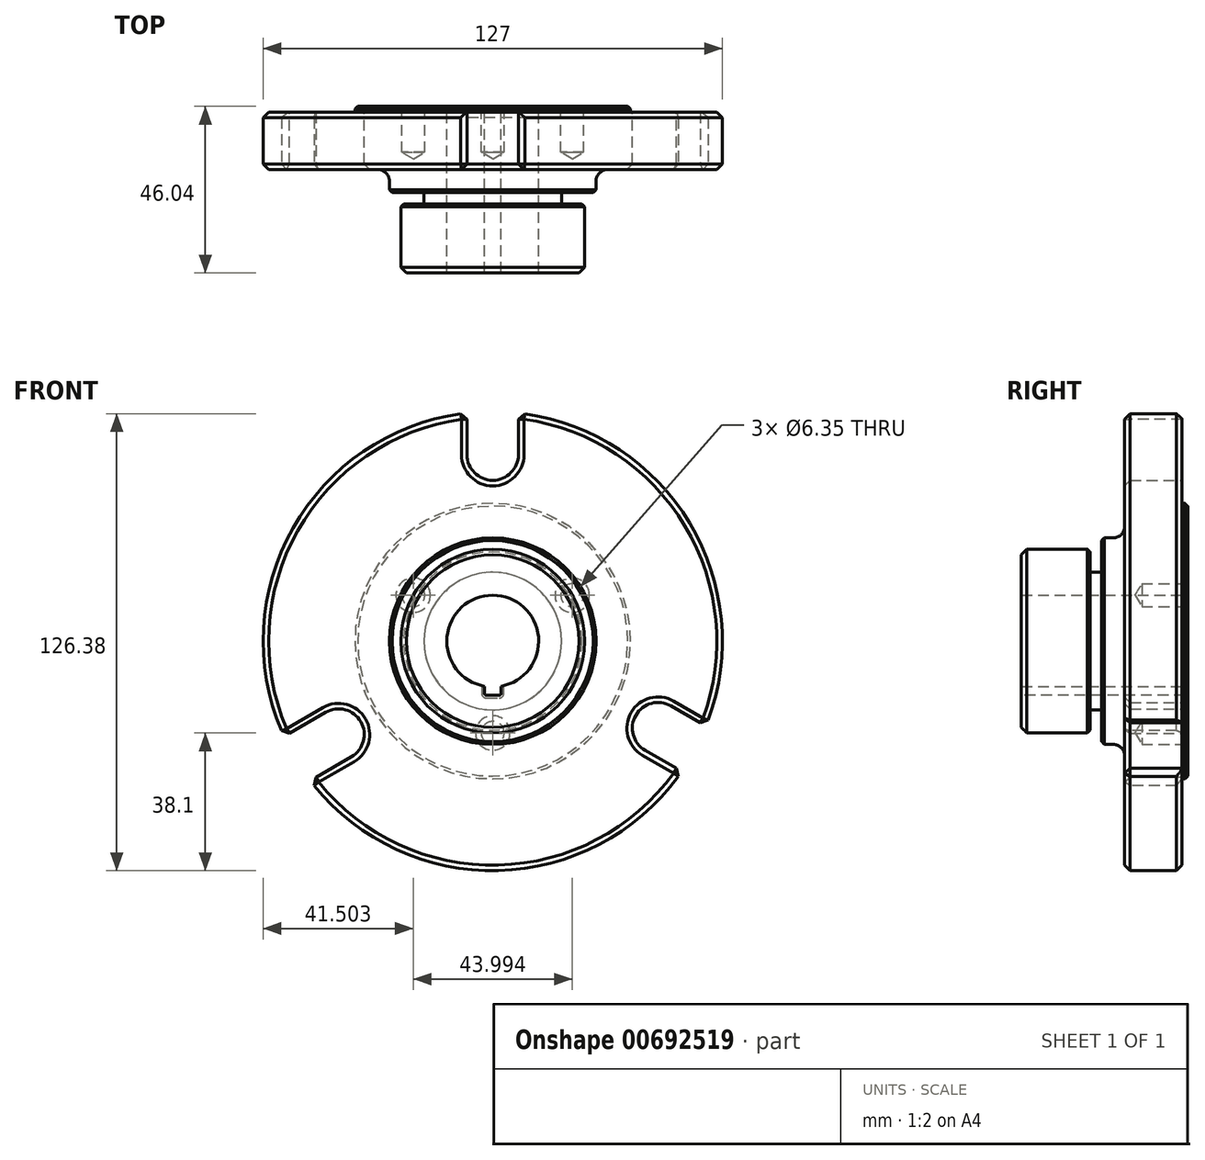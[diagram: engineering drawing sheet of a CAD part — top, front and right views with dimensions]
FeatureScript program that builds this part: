
annotation { "Feature Type Name" : "Feature", "Feature Type Description" : "" }
export const myFeature = defineFeature(function(context is Context, id is Id, definition is map)
    precondition{}
    {
        {
            var Q0;
            Q0=qCreatedBy(makeId("Right.planeOp"),FACE);
            var sketch = newSketch(context, id + "F0", { "sketchPlane" : qUnion([Q0])});
            skLineSegment(sketch, "E0", {"start": v(-17.46, 63.5) * mm, "end": v(-1.59, 63.5) * mm});
            skLineSegment(sketch, "E1", {"start": v(-1.59, 63.5) * mm, "end": v(-1.59, 38.1) * mm});
            skLineSegment(sketch, "E2", {"start": v(-1.59, 38.1) * mm, "end": v(0, 38.1) * mm});
            skLineSegment(sketch, "E3", {"start": v(0, 38.1) * mm, "end": v(0, 0) * mm});
            skLineSegment(sketch, "E4", {"start": v(0, 0) * mm, "end": v(-46.04, 0) * mm});
            skLineSegment(sketch, "E5", {"start": v(-46.04, 0) * mm, "end": v(-46.04, 25.4) * mm});
            skLineSegment(sketch, "E6", {"start": v(-46.04, 25.4) * mm, "end": v(-26.99, 25.4) * mm});
            skLineSegment(sketch, "E7", {"start": v(-26.99, 25.4) * mm, "end": v(-26.99, 19.05) * mm});
            skLineSegment(sketch, "E8", {"start": v(-26.99, 19.05) * mm, "end": v(-23.81, 19.05) * mm});
            skLineSegment(sketch, "E9", {"start": v(-23.81, 19.05) * mm, "end": v(-23.81, 28.58) * mm});
            skLineSegment(sketch, "E10", {"start": v(-23.81, 28.58) * mm, "end": v(-20.64, 28.58) * mm});
            skLineSegment(sketch, "E11", {"start": v(-17.46, 31.75) * mm, "end": v(-17.46, 63.5) * mm});
            skPoint(sketch, "E12.visualSharp", {"position": v(-17.46, 28.58) * mm});
            skArc(sketch, "E12.filletArc", {"start": v(-20.64, 28.57) * mm, "mid": v(-18.4, 29.5) * mm, "end": v(-17.46, 31.75) * mm});
            skLineSegment(sketch, "E13", {"start": v(-69.6, 0) * mm, "end": v(49.13, 0) * mm, "construction": true});
            skSolve(sketch);
        }
        {
            var Q0;
            Q0=makeQuery(id+"F0.imprint","IMPRINT",FACE,{"disambiguationData":[TD([[makeQuery(id+"F0.imprint","IMPRINT",EDGE,{"derivedFrom":sQuery(id+"F0.wireOp",EDGE,"E0")}),-1.0]])]});
            var Q1;
            Q1=sQuery(id+"F0.wireOp",EDGE,"E13");
            revolve(context, id + "F1", {"entities" : qUnion([Q0]), "axis" : qUnion([Q1]), "revolveType" : RevolveType.FULL});
        }
        {
            var Q0;
            Q0=makeQuery(id+"F1.opRevolve","SWEPT_FACE",FACE,{"disambiguationData":[OSD([sQuery(id+"F0.wireOp",EDGE,"E3")])]});
            var sketch = newSketch(context, id + "F2", { "sketchPlane" : qUnion([Q0])});
            skPoint(sketch, "E14", {"position": v(0, 0) * mm});
            skSolve(sketch);
        }
        {
            var Q0;
            Q0=sQuery(id+"F2.wireOp",VERTEX,"E14");
            var Q1;
            Q1=makeQuery(id+"F1.opRevolve","SWEPT_BODY",BODY,{"disambiguationData":[OSD([sQuery(id+"F0.wireOp",EDGE,"E0"),sQuery(id+"F0.wireOp",EDGE,"E1"),sQuery(id+"F0.wireOp",EDGE,"E2"),sQuery(id+"F0.wireOp",EDGE,"E3"),sQuery(id+"F0.wireOp",EDGE,"E4"),sQuery(id+"F0.wireOp",EDGE,"E5"),sQuery(id+"F0.wireOp",EDGE,"E6"),sQuery(id+"F0.wireOp",EDGE,"E7"),sQuery(id+"F0.wireOp",EDGE,"E8"),sQuery(id+"F0.wireOp",EDGE,"E9"),sQuery(id+"F0.wireOp",EDGE,"E10"),sQuery(id+"F0.wireOp",EDGE,"E11"),sQuery(id+"F0.wireOp",EDGE,"E12.filletArc")])]});
            hole(context, id + "F3", {"style" : HoleStyle.SIMPLE, "endStyle" : HoleEndStyle.THROUGH, "holeDiameter" : 25.4 * mm, "majorDiameter" : 6.35 * mm, "isTappedThrough" : true, "tappedDepth" : 12.7 * mm, "tapClearance" : 3, "locations" : qUnion([Q0]), "scope" : qUnion([Q1])});
        }
        {
            var Q0;
            Q0=makeQuery(id+"F1.opRevolve","SWEPT_FACE",FACE,{"disambiguationData":[OSD([sQuery(id+"F0.wireOp",EDGE,"E1")])]});
            var sketch = newSketch(context, id + "F4", { "sketchPlane" : qUnion([Q0])});
            skCircle(sketch, "E15", {"center": v(0, 0) * mm, "radius": 51.6 * mm, "construction": true});
            skLineSegment(sketch, "E16", {"start": v(0, 0) * mm, "end": v(0, 88.74) * mm, "construction": true});
            skLineSegment(sketch, "E17", {"start": v(0, 0) * mm, "end": v(99.06, 0) * mm, "construction": true});
            skLineSegment(sketch, "E18.bottom", {"start": v(7.11, 51.6) * mm, "end": v(-7.11, 51.6) * mm, "construction": true});
            skLineSegment(sketch, "E18.top", {"start": v(7.11, 76.2) * mm, "end": v(-7.11, 76.2) * mm});
            skLineSegment(sketch, "E18.left", {"start": v(7.11, 51.6) * mm, "end": v(7.11, 76.2) * mm});
            skLineSegment(sketch, "E18.right", {"start": v(-7.11, 51.6) * mm, "end": v(-7.11, 76.2) * mm});
            skPoint(sketch, "E18.middle", {"position": v(0, 63.9) * mm});
            skArc(sketch, "E19", {"start": v(-7.11, 51.6) * mm, "mid": v(0, 44.48) * mm, "end": v(7.11, 51.6) * mm});
            skPoint(sketch, "E20.1.0", {"position": v(-56.4, -30.22) * mm});
            skLineSegment(sketch, "E20.1.1", {"start": v(-70.6, -30.22) * mm, "end": v(-63.5, -42.54) * mm});
            skLineSegment(sketch, "E20.1.2", {"start": v(-49.3, -17.91) * mm, "end": v(-70.6, -30.22) * mm});
            skLineSegment(sketch, "E20.1.3", {"start": v(-42.18, -30.23) * mm, "end": v(-63.5, -42.54) * mm});
            skArc(sketch, "E20.1.4", {"start": v(-42.18, -30.23) * mm, "mid": v(-39.58, -20.52) * mm, "end": v(-49.3, -17.91) * mm});
            skLineSegment(sketch, "E20.1.5", {"start": v(-49.3, -17.91) * mm, "end": v(-42.18, -30.23) * mm, "construction": true});
            skPoint(sketch, "E20.2.0", {"position": v(53.31, -32) * mm});
            skLineSegment(sketch, "E20.2.1", {"start": v(60.41, -44.31) * mm, "end": v(67.52, -32) * mm});
            skLineSegment(sketch, "E20.2.2", {"start": v(39.1, -32.01) * mm, "end": v(60.41, -44.31) * mm});
            skLineSegment(sketch, "E20.2.3", {"start": v(46.22, -19.7) * mm, "end": v(67.52, -32) * mm});
            skArc(sketch, "E20.2.4", {"start": v(46.22, -19.7) * mm, "mid": v(36.5, -22.3) * mm, "end": v(39.1, -32.01) * mm});
            skLineSegment(sketch, "E20.2.5", {"start": v(39.1, -32.01) * mm, "end": v(46.22, -19.7) * mm, "construction": true});
            skPoint(sketch, "E20.center", {"position": v(-1.03, 0.56) * mm});
            skSolve(sketch);
        }
        {
            var Q0;
            {var subQ0=sQuery(id+"F4.wireOp",EDGE,"E18.top");Q0=makeQuery(id+"F4.imprint","IMPRINT",FACE,{"disambiguationData":[TD([[makeQuery(id+"F4.imprint","IMPRINT",EDGE,{"derivedFrom":subQ0}),1.0]])]});}
            var Q1;
            {var subQ0=sQuery(id+"F4.wireOp",EDGE,"E19");Q1=makeQuery(id+"F4.imprint","IMPRINT",FACE,{"disambiguationData":[TD([[makeQuery(id+"F4.imprint","IMPRINT",EDGE,{"derivedFrom":subQ0}),1.0]])]});}
            var Q2;
            {var subQ0=sQuery(id+"F4.wireOp",EDGE,"E20.1.1");Q2=makeQuery(id+"F4.imprint","IMPRINT",FACE,{"disambiguationData":[TD([[makeQuery(id+"F4.imprint","IMPRINT",EDGE,{"derivedFrom":subQ0}),1.0]])]});}
            var Q3;
            {var subQ0=sQuery(id+"F4.wireOp",EDGE,"E20.1.4");Q3=makeQuery(id+"F4.imprint","IMPRINT",FACE,{"disambiguationData":[TD([[makeQuery(id+"F4.imprint","IMPRINT",EDGE,{"derivedFrom":subQ0}),1.0]])]});}
            var Q4;
            {var subQ0=sQuery(id+"F4.wireOp",EDGE,"E20.2.4");Q4=makeQuery(id+"F4.imprint","IMPRINT",FACE,{"disambiguationData":[TD([[makeQuery(id+"F4.imprint","IMPRINT",EDGE,{"derivedFrom":subQ0}),1.0]])]});}
            var Q5;
            {var subQ0=sQuery(id+"F4.wireOp",EDGE,"E20.2.1");Q5=makeQuery(id+"F4.imprint","IMPRINT",FACE,{"disambiguationData":[TD([[makeQuery(id+"F4.imprint","IMPRINT",EDGE,{"derivedFrom":subQ0}),1.0]])]});}
            extrude(context, id + "F5", {"entities" : qUnion([Q0, Q1, Q2, Q3, Q4, Q5]), "operationType" : NewBodyOperationType.REMOVE, "endBound" : BoundingType.THROUGH_ALL, "oppositeDirection" : true, "depth" : 25.4 * mm, "offsetDistance" : 25.4 * mm});
        }
        {
            var Q0;
            Q0=makeQuery(id+"F1.opRevolve","SWEPT_EDGE",EDGE,{"disambiguationData":[OSD([sQuery(id+"F0.wireOp",EDGE,"E2"),sQuery(id+"F0.wireOp",EDGE,"E3")])]});
            var Q1;
            Q1=makeQuery(id+"F3.hole-0.boolean.opBoolean","COPY",EDGE,{"derivedFrom":makeQuery(id+"F3.hole-0.opRevolve","SWEPT_EDGE",EDGE,{"disambiguationData":[OSD([sQuery(id+"F3.hole-0.sketch.wireOp",EDGE,"core_line_2"),sQuery(id+"F3.hole-0.sketch.wireOp",EDGE,"core_line_3")])]})});
            var Q2;
            Q2=makeQuery(id+"F3.hole-0.boolean.opBoolean","INTERSECT",EDGE,{"derivedFrom":[makeQuery(id+"F1.opRevolve","SWEPT_FACE",FACE,{"disambiguationData":[OSD([sQuery(id+"F0.wireOp",EDGE,"E5")])]}),makeQuery(id+"F3.hole-0.opRevolve","SWEPT_FACE",FACE,{"disambiguationData":[OSD([sQuery(id+"F3.hole-0.sketch.wireOp",EDGE,"core_line_2")])]})]});
            var Q3;
            Q3=makeQuery(id+"F1.opRevolve","SWEPT_EDGE",EDGE,{"disambiguationData":[OSD([sQuery(id+"F0.wireOp",EDGE,"E6"),sQuery(id+"F0.wireOp",EDGE,"E7")])]});
            var Q4;
            Q4=makeQuery(id+"F1.opRevolve","SWEPT_EDGE",EDGE,{"disambiguationData":[OSD([sQuery(id+"F0.wireOp",EDGE,"E9"),sQuery(id+"F0.wireOp",EDGE,"E10")])]});
            chamfer(context, id + "F6", {"entities" : qUnion([Q0, Q1, Q2, Q3, Q4]), "width" : 0.76 * mm, "tangentPropagation" : true});
        }
        {
            var Q0;
            Q0=makeQuery(id+"F1.opRevolve","SWEPT_EDGE",EDGE,{"disambiguationData":[OSD([sQuery(id+"F0.wireOp",EDGE,"E5"),sQuery(id+"F0.wireOp",EDGE,"E6")])]});
            var Q1;
            Q1=makeQuery(id+"F5.boolean.opBoolean","INTERSECT",EDGE,{"derivedFrom":[makeQuery(id+"F1.opRevolve","SWEPT_FACE",FACE,{"disambiguationData":[OSD([sQuery(id+"F0.wireOp",EDGE,"E11")])]}),makeQuery(id+"F5.opExtrude","SWEPT_FACE",FACE,{"disambiguationData":[OSD([sQuery(id+"F4.wireOp",EDGE,"E19")])]})]});
            var Q2;
            Q2=makeQuery(id+"F5.boolean.opBoolean","INTERSECT",EDGE,{"derivedFrom":[makeQuery(id+"F1.opRevolve","SWEPT_FACE",FACE,{"disambiguationData":[OSD([sQuery(id+"F0.wireOp",EDGE,"E11")])]}),makeQuery(id+"F5.opExtrude","SWEPT_FACE",FACE,{"disambiguationData":[OSD([sQuery(id+"F4.wireOp",EDGE,"E18.right")])]})]});
            var Q3;
            Q3=makeQuery(id+"F5.boolean.opBoolean","INTERSECT",EDGE,{"derivedFrom":[makeQuery(id+"F1.opRevolve","SWEPT_FACE",FACE,{"disambiguationData":[OSD([sQuery(id+"F0.wireOp",EDGE,"E11")])]}),makeQuery(id+"F5.opExtrude","SWEPT_FACE",FACE,{"disambiguationData":[OSD([sQuery(id+"F4.wireOp",EDGE,"E18.left")])]})]});
            var Q4;
            {var subQ0=sQuery(id+"F0.wireOp",EDGE,"E0");var subQ1=sQuery(id+"F0.wireOp",EDGE,"E11");Q4=makeQuery(id+"F5.boolean.opBoolean","SPLIT",EDGE,{"disambiguationData":[TD([makeQuery(id+"F5.opExtrude","SWEPT_FACE",FACE,{"disambiguationData":[OSD([sQuery(id+"F4.wireOp",EDGE,"E18.left")])]})])],"derivedFrom":makeQuery(id+"F1.opRevolve","SWEPT_EDGE",EDGE,{"disambiguationData":[OSD([subQ0,subQ1])]})});}
            var Q5;
            {var subQ0=sQuery(id+"F0.wireOp",EDGE,"E0");var subQ1=sQuery(id+"F0.wireOp",EDGE,"E11");Q5=makeQuery(id+"F5.boolean.opBoolean","SPLIT",EDGE,{"disambiguationData":[TD([makeQuery(id+"F5.opExtrude","SWEPT_FACE",FACE,{"disambiguationData":[OSD([sQuery(id+"F4.wireOp",EDGE,"E18.right")])]})])],"derivedFrom":makeQuery(id+"F1.opRevolve","SWEPT_EDGE",EDGE,{"disambiguationData":[OSD([subQ0,subQ1])]})});}
            var Q6;
            {var subQ0=sQuery(id+"F0.wireOp",EDGE,"E0");var subQ1=sQuery(id+"F0.wireOp",EDGE,"E11");Q6=makeQuery(id+"F5.boolean.opBoolean","SPLIT",EDGE,{"disambiguationData":[TD([makeQuery(id+"F5.opExtrude","SWEPT_FACE",FACE,{"disambiguationData":[OSD([sQuery(id+"F4.wireOp",EDGE,"E20.1.3")])]})])],"derivedFrom":makeQuery(id+"F1.opRevolve","SWEPT_EDGE",EDGE,{"disambiguationData":[OSD([subQ0,subQ1])]})});}
            var Q7;
            Q7=makeQuery(id+"F5.boolean.opBoolean","INTERSECT",EDGE,{"derivedFrom":[makeQuery(id+"F1.opRevolve","SWEPT_FACE",FACE,{"disambiguationData":[OSD([sQuery(id+"F0.wireOp",EDGE,"E11")])]}),makeQuery(id+"F5.opExtrude","SWEPT_FACE",FACE,{"disambiguationData":[OSD([sQuery(id+"F4.wireOp",EDGE,"E20.2.2")])]})]});
            var Q8;
            Q8=makeQuery(id+"F5.boolean.opBoolean","INTERSECT",EDGE,{"derivedFrom":[makeQuery(id+"F1.opRevolve","SWEPT_FACE",FACE,{"disambiguationData":[OSD([sQuery(id+"F0.wireOp",EDGE,"E11")])]}),makeQuery(id+"F5.opExtrude","SWEPT_FACE",FACE,{"disambiguationData":[OSD([sQuery(id+"F4.wireOp",EDGE,"E20.2.4")])]})]});
            var Q9;
            Q9=makeQuery(id+"F5.boolean.opBoolean","INTERSECT",EDGE,{"derivedFrom":[makeQuery(id+"F1.opRevolve","SWEPT_FACE",FACE,{"disambiguationData":[OSD([sQuery(id+"F0.wireOp",EDGE,"E11")])]}),makeQuery(id+"F5.opExtrude","SWEPT_FACE",FACE,{"disambiguationData":[OSD([sQuery(id+"F4.wireOp",EDGE,"E20.2.3")])]})]});
            var Q10;
            Q10=makeQuery(id+"F5.boolean.opBoolean","INTERSECT",EDGE,{"derivedFrom":[makeQuery(id+"F1.opRevolve","SWEPT_FACE",FACE,{"disambiguationData":[OSD([sQuery(id+"F0.wireOp",EDGE,"E11")])]}),makeQuery(id+"F5.opExtrude","SWEPT_FACE",FACE,{"disambiguationData":[OSD([sQuery(id+"F4.wireOp",EDGE,"E20.1.3")])]})]});
            var Q11;
            Q11=makeQuery(id+"F5.boolean.opBoolean","INTERSECT",EDGE,{"derivedFrom":[makeQuery(id+"F1.opRevolve","SWEPT_FACE",FACE,{"disambiguationData":[OSD([sQuery(id+"F0.wireOp",EDGE,"E11")])]}),makeQuery(id+"F5.opExtrude","SWEPT_FACE",FACE,{"disambiguationData":[OSD([sQuery(id+"F4.wireOp",EDGE,"E20.1.2")])]})]});
            var Q12;
            Q12=makeQuery(id+"F5.boolean.opBoolean","INTERSECT",EDGE,{"derivedFrom":[makeQuery(id+"F1.opRevolve","SWEPT_FACE",FACE,{"disambiguationData":[OSD([sQuery(id+"F0.wireOp",EDGE,"E11")])]}),makeQuery(id+"F5.opExtrude","SWEPT_FACE",FACE,{"disambiguationData":[OSD([sQuery(id+"F4.wireOp",EDGE,"E20.1.4")])]})]});
            var Q13;
            {var subQ0=sQuery(id+"F0.wireOp",EDGE,"E0");var subQ1=sQuery(id+"F0.wireOp",EDGE,"E1");Q13=makeQuery(id+"F5.boolean.opBoolean","SPLIT",EDGE,{"disambiguationData":[TD([makeQuery(id+"F5.opExtrude","SWEPT_FACE",FACE,{"disambiguationData":[OSD([sQuery(id+"F4.wireOp",EDGE,"E18.right")])]})])],"derivedFrom":makeQuery(id+"F1.opRevolve","SWEPT_EDGE",EDGE,{"disambiguationData":[OSD([subQ0,subQ1])]})});}
            var Q14;
            Q14=makeQuery(id+"F5.boolean.opBoolean","COPY",EDGE,{"derivedFrom":makeQuery(id+"F5.opExtrude","CAP_EDGE",EDGE,{"disambiguationData":[OSD([sQuery(id+"F4.wireOp",EDGE,"E20.1.2")])],"isStart":true})});
            var Q15;
            Q15=makeQuery(id+"F5.boolean.opBoolean","COPY",EDGE,{"derivedFrom":makeQuery(id+"F5.opExtrude","CAP_EDGE",EDGE,{"disambiguationData":[OSD([sQuery(id+"F4.wireOp",EDGE,"E20.1.4")])],"isStart":true})});
            var Q16;
            Q16=makeQuery(id+"F5.boolean.opBoolean","COPY",EDGE,{"derivedFrom":makeQuery(id+"F5.opExtrude","CAP_EDGE",EDGE,{"disambiguationData":[OSD([sQuery(id+"F4.wireOp",EDGE,"E20.1.3")])],"isStart":true})});
            var Q17;
            {var subQ0=sQuery(id+"F0.wireOp",EDGE,"E0");var subQ1=sQuery(id+"F0.wireOp",EDGE,"E1");Q17=makeQuery(id+"F5.boolean.opBoolean","SPLIT",EDGE,{"disambiguationData":[TD([makeQuery(id+"F5.opExtrude","SWEPT_FACE",FACE,{"disambiguationData":[OSD([sQuery(id+"F4.wireOp",EDGE,"E20.1.3")])]})])],"derivedFrom":makeQuery(id+"F1.opRevolve","SWEPT_EDGE",EDGE,{"disambiguationData":[OSD([subQ0,subQ1])]})});}
            var Q18;
            Q18=makeQuery(id+"F5.boolean.opBoolean","COPY",EDGE,{"derivedFrom":makeQuery(id+"F5.opExtrude","CAP_EDGE",EDGE,{"disambiguationData":[OSD([sQuery(id+"F4.wireOp",EDGE,"E20.2.2")])],"isStart":true})});
            var Q19;
            Q19=makeQuery(id+"F5.boolean.opBoolean","COPY",EDGE,{"derivedFrom":makeQuery(id+"F5.opExtrude","CAP_EDGE",EDGE,{"disambiguationData":[OSD([sQuery(id+"F4.wireOp",EDGE,"E20.2.3")])],"isStart":true})});
            var Q20;
            Q20=makeQuery(id+"F5.boolean.opBoolean","COPY",EDGE,{"derivedFrom":makeQuery(id+"F5.opExtrude","CAP_EDGE",EDGE,{"disambiguationData":[OSD([sQuery(id+"F4.wireOp",EDGE,"E20.2.4")])],"isStart":true})});
            var Q21;
            {var subQ0=sQuery(id+"F0.wireOp",EDGE,"E0");var subQ1=sQuery(id+"F0.wireOp",EDGE,"E1");Q21=makeQuery(id+"F5.boolean.opBoolean","SPLIT",EDGE,{"disambiguationData":[TD([makeQuery(id+"F5.opExtrude","SWEPT_FACE",FACE,{"disambiguationData":[OSD([sQuery(id+"F4.wireOp",EDGE,"E18.left")])]})])],"derivedFrom":makeQuery(id+"F1.opRevolve","SWEPT_EDGE",EDGE,{"disambiguationData":[OSD([subQ0,subQ1])]})});}
            var Q22;
            Q22=makeQuery(id+"F5.boolean.opBoolean","COPY",EDGE,{"derivedFrom":makeQuery(id+"F5.opExtrude","CAP_EDGE",EDGE,{"disambiguationData":[OSD([sQuery(id+"F4.wireOp",EDGE,"E18.left")])],"isStart":true})});
            var Q23;
            Q23=makeQuery(id+"F5.boolean.opBoolean","COPY",EDGE,{"derivedFrom":makeQuery(id+"F5.opExtrude","CAP_EDGE",EDGE,{"disambiguationData":[OSD([sQuery(id+"F4.wireOp",EDGE,"E19")])],"isStart":true})});
            var Q24;
            Q24=makeQuery(id+"F5.boolean.opBoolean","COPY",EDGE,{"derivedFrom":makeQuery(id+"F5.opExtrude","CAP_EDGE",EDGE,{"disambiguationData":[OSD([sQuery(id+"F4.wireOp",EDGE,"E18.right")])],"isStart":true})});
            var Q25;
            Q25=makeQuery(id+"F5.boolean.opBoolean","INTERSECT",EDGE,{"derivedFrom":[makeQuery(id+"F1.opRevolve","SWEPT_FACE",FACE,{"disambiguationData":[OSD([sQuery(id+"F0.wireOp",EDGE,"E0")])]}),makeQuery(id+"F5.opExtrude","SWEPT_FACE",FACE,{"disambiguationData":[OSD([sQuery(id+"F4.wireOp",EDGE,"E18.left")])]})]});
            var Q26;
            Q26=makeQuery(id+"F5.boolean.opBoolean","INTERSECT",EDGE,{"derivedFrom":[makeQuery(id+"F1.opRevolve","SWEPT_FACE",FACE,{"disambiguationData":[OSD([sQuery(id+"F0.wireOp",EDGE,"E0")])]}),makeQuery(id+"F5.opExtrude","SWEPT_FACE",FACE,{"disambiguationData":[OSD([sQuery(id+"F4.wireOp",EDGE,"E18.right")])]})]});
            var Q27;
            Q27=makeQuery(id+"F5.boolean.opBoolean","INTERSECT",EDGE,{"derivedFrom":[makeQuery(id+"F1.opRevolve","SWEPT_FACE",FACE,{"disambiguationData":[OSD([sQuery(id+"F0.wireOp",EDGE,"E0")])]}),makeQuery(id+"F5.opExtrude","SWEPT_FACE",FACE,{"disambiguationData":[OSD([sQuery(id+"F4.wireOp",EDGE,"E20.1.2")])]})]});
            var Q28;
            Q28=makeQuery(id+"F5.boolean.opBoolean","INTERSECT",EDGE,{"derivedFrom":[makeQuery(id+"F1.opRevolve","SWEPT_FACE",FACE,{"disambiguationData":[OSD([sQuery(id+"F0.wireOp",EDGE,"E0")])]}),makeQuery(id+"F5.opExtrude","SWEPT_FACE",FACE,{"disambiguationData":[OSD([sQuery(id+"F4.wireOp",EDGE,"E20.1.3")])]})]});
            var Q29;
            Q29=makeQuery(id+"F5.boolean.opBoolean","INTERSECT",EDGE,{"derivedFrom":[makeQuery(id+"F1.opRevolve","SWEPT_FACE",FACE,{"disambiguationData":[OSD([sQuery(id+"F0.wireOp",EDGE,"E0")])]}),makeQuery(id+"F5.opExtrude","SWEPT_FACE",FACE,{"disambiguationData":[OSD([sQuery(id+"F4.wireOp",EDGE,"E20.2.2")])]})]});
            var Q30;
            Q30=makeQuery(id+"F5.boolean.opBoolean","INTERSECT",EDGE,{"derivedFrom":[makeQuery(id+"F1.opRevolve","SWEPT_FACE",FACE,{"disambiguationData":[OSD([sQuery(id+"F0.wireOp",EDGE,"E0")])]}),makeQuery(id+"F5.opExtrude","SWEPT_FACE",FACE,{"disambiguationData":[OSD([sQuery(id+"F4.wireOp",EDGE,"E20.2.3")])]})]});
            chamfer(context, id + "F7", {"entities" : qUnion([Q0, Q1, Q2, Q3, Q4, Q5, Q6, Q7, Q8, Q9, Q10, Q11, Q12, Q13, Q14, Q15, Q16, Q17, Q18, Q19, Q20, Q21, Q22, Q23, Q24, Q25, Q26, Q27, Q28, Q29, Q30]), "width" : 1.52 * mm, "tangentPropagation" : true});
        }
        {
            var Q0;
            Q0=makeQuery(id+"F1.opRevolve","SWEPT_EDGE",EDGE,{"disambiguationData":[OSD([sQuery(id+"F0.wireOp",EDGE,"E7"),sQuery(id+"F0.wireOp",EDGE,"E8")])]});
            var Q1;
            Q1=makeQuery(id+"F1.opRevolve","SWEPT_EDGE",EDGE,{"disambiguationData":[OSD([sQuery(id+"F0.wireOp",EDGE,"E8"),sQuery(id+"F0.wireOp",EDGE,"E9")])]});
            fillet(context, id + "F8", {"entities" : qUnion([Q0, Q1]), "radius" : 0.5 * mm, "tangentPropagation" : true, "allowEdgeOverflow" : false});
        }
        {
            var Q0;
            Q0=makeQuery(id+"F1.opRevolve","SWEPT_FACE",FACE,{"disambiguationData":[OSD([sQuery(id+"F0.wireOp",EDGE,"E3")])]});
            var sketch = newSketch(context, id + "F9", { "sketchPlane" : qUnion([Q0])});
            skCircle(sketch, "E21", {"center": v(0, 0) * mm, "radius": 25.4 * mm, "construction": true});
            skLineSegment(sketch, "E22", {"start": v(0, 0) * mm, "end": v(0, 71.25) * mm, "construction": true});
            skLineSegment(sketch, "E23", {"start": v(0, 0) * mm, "end": v(22, 12.7) * mm, "construction": true});
            skLineSegment(sketch, "E24.1.0", {"start": v(0, 0) * mm, "end": v(-22, 12.7) * mm, "construction": true});
            skLineSegment(sketch, "E24.2.0", {"start": v(0, 0) * mm, "end": v(0, -25.4) * mm, "construction": true});
            skSolve(sketch);
        }
        {
            var Q0;
            Q0=sQuery(id+"F9.wireOp",VERTEX,"E23.end");
            var Q1;
            Q1=sQuery(id+"F9.wireOp",VERTEX,"E24.1.0.end");
            var Q2;
            Q2=sQuery(id+"F9.wireOp",VERTEX,"E24.2.0.end");
            var Q3;
            Q3=makeQuery(id+"F1.opRevolve","SWEPT_BODY",BODY,{"disambiguationData":[OSD([sQuery(id+"F0.wireOp",EDGE,"E0"),sQuery(id+"F0.wireOp",EDGE,"E1"),sQuery(id+"F0.wireOp",EDGE,"E2"),sQuery(id+"F0.wireOp",EDGE,"E3"),sQuery(id+"F0.wireOp",EDGE,"E4"),sQuery(id+"F0.wireOp",EDGE,"E5"),sQuery(id+"F0.wireOp",EDGE,"E6"),sQuery(id+"F0.wireOp",EDGE,"E7"),sQuery(id+"F0.wireOp",EDGE,"E8"),sQuery(id+"F0.wireOp",EDGE,"E9"),sQuery(id+"F0.wireOp",EDGE,"E10"),sQuery(id+"F0.wireOp",EDGE,"E11"),sQuery(id+"F0.wireOp",EDGE,"E12.filletArc")])]});
            hole(context, id + "F10", {"style" : HoleStyle.C_SINK, "endStyle" : HoleEndStyle.BLIND, "holeDiameter" : 6.35 * mm, "cSinkDiameter" : 9.52 * mm, "cSinkAngle" : 90 * degree, "majorDiameter" : 6.35 * mm, "holeDepth" : 12.7 * mm, "isTappedThrough" : true, "tappedDepth" : 12.7 * mm, "tapClearance" : 3, "locations" : qUnion([Q0, Q1, Q2]), "scope" : qUnion([Q3])});
        }
        {
            var Q0;
            Q0=makeQuery(id+"F1.opRevolve","SWEPT_FACE",FACE,{"disambiguationData":[OSD([sQuery(id+"F0.wireOp",EDGE,"E5")])]});
            var sketch = newSketch(context, id + "F11", { "sketchPlane" : qUnion([Q0])});
            skLineSegment(sketch, "E25.bottom", {"start": v(1.78, -14.99) * mm, "end": v(-1.78, -14.99) * mm});
            skLineSegment(sketch, "E25.top", {"start": v(2.29, -5.46) * mm, "end": v(-2.29, -5.46) * mm});
            skLineSegment(sketch, "E25.left", {"start": v(2.29, -14.48) * mm, "end": v(2.29, -5.46) * mm});
            skLineSegment(sketch, "E25.right", {"start": v(-2.29, -14.48) * mm, "end": v(-2.29, -5.46) * mm});
            skPoint(sketch, "E25.middle", {"position": v(0, -10.22) * mm});
            skPoint(sketch, "E26.visualSharp", {"position": v(-2.29, -14.99) * mm});
            skArc(sketch, "E26.filletArc", {"start": v(-2.29, -14.48) * mm, "mid": v(-2.14, -14.84) * mm, "end": v(-1.78, -14.99) * mm});
            skPoint(sketch, "E27.visualSharp", {"position": v(2.29, -14.99) * mm});
            skArc(sketch, "E27.filletArc", {"start": v(1.78, -14.99) * mm, "mid": v(2.14, -14.84) * mm, "end": v(2.29, -14.48) * mm});
            skSolve(sketch);
        }
        {
            var Q0;
            Q0=makeQuery(id+"F11.imprint","IMPRINT",FACE,{"disambiguationData":[TD([[makeQuery(id+"F11.imprint","IMPRINT",EDGE,{"derivedFrom":sQuery(id+"F11.wireOp",EDGE,"E25.bottom")}),-1.0]])]});
            var Q1;
            {var subQ0=sQuery(id+"F11.wireOp",EDGE,"E25.top");Q1=makeQuery(id+"F11.imprint","IMPRINT",FACE,{"disambiguationData":[TD([[makeQuery(id+"F11.imprint","IMPRINT",EDGE,{"derivedFrom":subQ0}),1.0]])]});}
            extrude(context, id + "F12", {"entities" : qUnion([Q0, Q1]), "operationType" : NewBodyOperationType.REMOVE, "endBound" : BoundingType.THROUGH_ALL, "oppositeDirection" : true, "depth" : 25.4 * mm, "offsetDistance" : 25.4 * mm});
        }
        {
            var Q0;
            Q0=makeQuery(id+"F12.boolean.opBoolean","COPY",EDGE,{"derivedFrom":makeQuery(id+"F12.opExtrude","CAP_EDGE",EDGE,{"disambiguationData":[OSD([sQuery(id+"F11.wireOp",EDGE,"E25.right")])],"isStart":true})});
            var Q1;
            Q1=makeQuery(id+"F12.boolean.opBoolean","INTERSECT",EDGE,{"derivedFrom":[makeQuery(id+"F1.opRevolve","SWEPT_FACE",FACE,{"disambiguationData":[OSD([sQuery(id+"F0.wireOp",EDGE,"E3")])]}),makeQuery(id+"F12.opExtrude","SWEPT_FACE",FACE,{"disambiguationData":[OSD([sQuery(id+"F11.wireOp",EDGE,"E25.bottom")])]})]});
            var Q2;
            Q2=makeQuery(id+"F12.boolean.opBoolean","INTERSECT",EDGE,{"derivedFrom":[makeQuery(id+"F3.hole-0.boolean.opBoolean","COPY",FACE,{"derivedFrom":makeQuery(id+"F3.hole-0.opRevolve","SWEPT_FACE",FACE,{"disambiguationData":[OSD([sQuery(id+"F3.hole-0.sketch.wireOp",EDGE,"core_line_2")])]})}),makeQuery(id+"F12.opExtrude","SWEPT_FACE",FACE,{"disambiguationData":[OSD([sQuery(id+"F11.wireOp",EDGE,"E25.right")])]})]});
            var Q3;
            Q3=makeQuery(id+"F12.boolean.opBoolean","INTERSECT",EDGE,{"derivedFrom":[makeQuery(id+"F3.hole-0.boolean.opBoolean","COPY",FACE,{"derivedFrom":makeQuery(id+"F3.hole-0.opRevolve","SWEPT_FACE",FACE,{"disambiguationData":[OSD([sQuery(id+"F3.hole-0.sketch.wireOp",EDGE,"core_line_2")])]})}),makeQuery(id+"F12.opExtrude","SWEPT_FACE",FACE,{"disambiguationData":[OSD([sQuery(id+"F11.wireOp",EDGE,"E25.left")])]})]});
            chamfer(context, id + "F13", {"entities" : qUnion([Q0, Q1, Q2, Q3]), "width" : 0.76 * mm, "tangentPropagation" : true});
        }
    });
